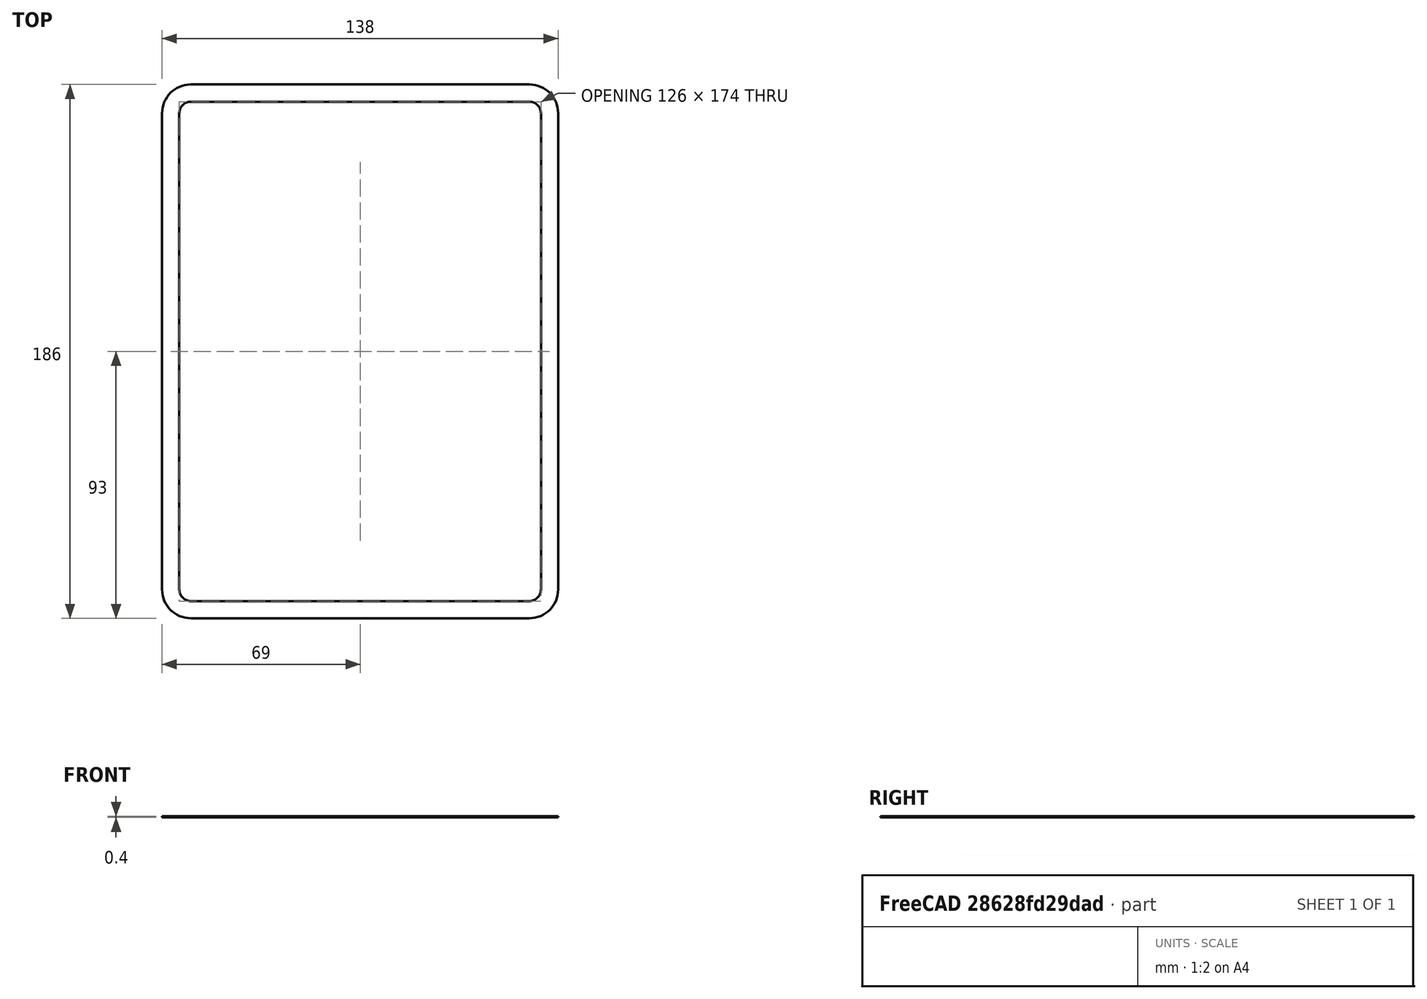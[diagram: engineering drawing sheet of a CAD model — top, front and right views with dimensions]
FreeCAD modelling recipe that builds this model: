
FCSTD DOCUMENT  (FreeCAD 0.21R33771 (Git))
Label: LidSeal
License: All rights reserved
LicenseURL: http://en.wikipedia.org/wiki/All_rights_reserved
objects: Sketcher::SketchObject×1, PartDesign::Pad×1, PartDesign::Body×1
note: 4 computed .brp shape members not serialized (recipe doc carries the construction recipe); baked Part::Feature solids carry a one-line shape summary decoded from their .brp

FEATURE [Sketcher::SketchObject] Sketch
  FullyConstrained = true
  MapMode = 5
  Support = -> [XY_Plane]
  sketch-geometry (29):
    g0: LineSegment StartX=-59 StartY=90 StartZ=0 EndX=59 EndY=90 EndZ=0
    g1: LineSegment StartX=66 StartY=83 StartZ=0 EndX=66 EndY=-83 EndZ=0
    g2: LineSegment StartX=59 StartY=-90 StartZ=0 EndX=-59 EndY=-90 EndZ=0
    g3: LineSegment StartX=-66 StartY=-83 StartZ=0 EndX=-66 EndY=83 EndZ=0
    g4: ArcOfCircle CenterX=-59 CenterY=83 CenterZ=0 NormalX=0 NormalY=0 NormalZ=1 AngleXU=0 Radius=7 StartAngle=1.5708 EndAngle=3.14159
    g5: ArcOfCircle CenterX=59 CenterY=83 CenterZ=0 NormalX=0 NormalY=0 NormalZ=1 AngleXU=0 Radius=7 StartAngle=4e-16 EndAngle=1.5708
    g6: ArcOfCircle CenterX=-59 CenterY=-83 CenterZ=0 NormalX=0 NormalY=0 NormalZ=1 AngleXU=0 Radius=7 StartAngle=3.14159 EndAngle=4.71239
    g7: ArcOfCircle CenterX=59 CenterY=-83 CenterZ=0 NormalX=0 NormalY=0 NormalZ=1 AngleXU=0 Radius=7 StartAngle=4.71239 EndAngle=6.28319
    g8: ArcOfCircle CenterX=-59 CenterY=83 CenterZ=0 NormalX=0 NormalY=0 NormalZ=1 AngleXU=0 Radius=10 StartAngle=1.5708 EndAngle=3.14159
    g9: LineSegment StartX=-59 StartY=93 StartZ=0 EndX=59 EndY=93 EndZ=0
    g10: ArcOfCircle CenterX=59 CenterY=83 CenterZ=0 NormalX=0 NormalY=0 NormalZ=1 AngleXU=0 Radius=10 StartAngle=7e-16 EndAngle=1.5708
    g11: LineSegment StartX=69 StartY=83 StartZ=0 EndX=69 EndY=-83 EndZ=0
    g12: ArcOfCircle CenterX=59 CenterY=-83 CenterZ=0 NormalX=0 NormalY=0 NormalZ=1 AngleXU=0 Radius=10 StartAngle=4.71239 EndAngle=6.28319
    g13: LineSegment StartX=59 StartY=-93 StartZ=0 EndX=-59 EndY=-93 EndZ=0
    g14: ArcOfCircle CenterX=-59 CenterY=-83 CenterZ=0 NormalX=0 NormalY=0 NormalZ=1 AngleXU=0 Radius=10 StartAngle=3.14159 EndAngle=4.71239
    g15: LineSegment StartX=-69 StartY=-83 StartZ=0 EndX=-69 EndY=83 EndZ=0
    g16: GeomPoint X=-69 Y=93 Z=0
    g17: GeomPoint X=69 Y=-93 Z=0
    g18: ArcOfCircle CenterX=-59 CenterY=83 CenterZ=0 NormalX=0 NormalY=0 NormalZ=1 AngleXU=0 Radius=4 StartAngle=1.5708 EndAngle=3.14159
    g19: LineSegment StartX=-59 StartY=87 StartZ=0 EndX=59 EndY=87 EndZ=0
    g20: ArcOfCircle CenterX=59 CenterY=83 CenterZ=0 NormalX=0 NormalY=0 NormalZ=1 AngleXU=0 Radius=4 StartAngle=9e-16 EndAngle=1.5708
    g21: LineSegment StartX=63 StartY=83 StartZ=0 EndX=63 EndY=-83 EndZ=0
    g22: ArcOfCircle CenterX=59 CenterY=-83 CenterZ=0 NormalX=0 NormalY=0 NormalZ=1 AngleXU=0 Radius=4 StartAngle=4.71239 EndAngle=6.28319
    g23: LineSegment StartX=59 StartY=-87 StartZ=0 EndX=-59 EndY=-87 EndZ=0
    g24: ArcOfCircle CenterX=-59 CenterY=-83 CenterZ=0 NormalX=0 NormalY=0 NormalZ=1 AngleXU=0 Radius=4 StartAngle=3.14159 EndAngle=4.71239
    g25: LineSegment StartX=-63 StartY=-83 StartZ=0 EndX=-63 EndY=83 EndZ=0
    g26: GeomPoint X=-63 Y=87 Z=0
    g27: GeomPoint X=63 Y=-87 Z=0
    g28: LineSegment StartX=-59 StartY=87 StartZ=0 EndX=-59 EndY=93 EndZ=0
  constraints (62):
    c: Horizontal(g0)
    c: Horizontal(g2)
    c: Vertical(g1)
    c: Vertical(g3)
    c: Tangent(g0,g4) = 1.5708
    c: Tangent(g3,g4) = 1.5708
    c: Tangent(g0,g5) = 1.5708
    c: Tangent(g1,g5) = 1.5708
    c: Tangent(g2,g6) = 1.5708
    c: Tangent(g3,g6) = 1.5708
    c: Tangent(g1,g7) = 1.5708
    c: Tangent(g2,g7) = 1.5708
    c: DistanceX(g3,g1) = 132
    c: DistanceY(g2,g0) = 180
    c: Equal(g5,g4)
    c: Radius(g4) = 7
    c: Symmetric(g6,g5,g-1)
    c: Tangent(g8,g9) = 1.5708
    c: Tangent(g9,g10) = 1.5708
    c: Tangent(g10,g11) = 1.5708
    c: Tangent(g11,g12) = 1.5708
    c: Tangent(g12,g13) = 1.5708
    c: Tangent(g13,g14) = 1.5708
    c: Tangent(g14,g15) = 1.5708
    c: Tangent(g15,g8) = 1.5708
    c: Horizontal(g9)
    c: Horizontal(g13)
    c: Vertical(g11)
    c: Vertical(g15)
    c: Equal(g8,g10)
    c: PointOnObject(g16,g9)
    c: PointOnObject(g16,g15)
    c: PointOnObject(g17,g11)
    c: PointOnObject(g17,g13)
    c: Tangent(g18,g19) = 1.5708
    c: Tangent(g19,g20) = 1.5708
    c: Tangent(g20,g21) = 1.5708
    c: Tangent(g21,g22) = 1.5708
    c: Tangent(g22,g23) = 1.5708
    c: Tangent(g23,g24) = 1.5708
    c: Tangent(g24,g25) = 1.5708
    c: Tangent(g25,g18) = 1.5708
    c: Horizontal(g23)
    c: Vertical(g21)
    c: Vertical(g25)
    c: Equal(g18,g20)
    c: PointOnObject(g26,g19)
    c: PointOnObject(g26,g25)
    c: PointOnObject(g27,g21)
    c: PointOnObject(g27,g23)
    c: Coincident(g22,g7)
    c: Coincident(g22,g12)
    c: Coincident(g24,g6)
    c: Coincident(g14,g24)
    c: Coincident(g8,g4)
    c: Coincident(g18,g8)
    c: Equal(g20,g22)
    c: Coincident(g28,g18)
    c: Coincident(g28,g8)
    c: Symmetric(g8,g18,g0)
    c: DistanceY(g18,g8) = 6
    c: Equal(g12,g14)
FEATURE [PartDesign::Pad] Pad
  Direction = (0,0,1)
  Length = 0.4
  Length2 = 10
  Profile = -> Sketch
  ReferenceAxis = -> Sketch [N_Axis]
  Type = 0
FEATURE [PartDesign::Body] Body
  Group = -> [Sketch,Pad]
  Origin = -> Origin
  Tip = -> Pad
